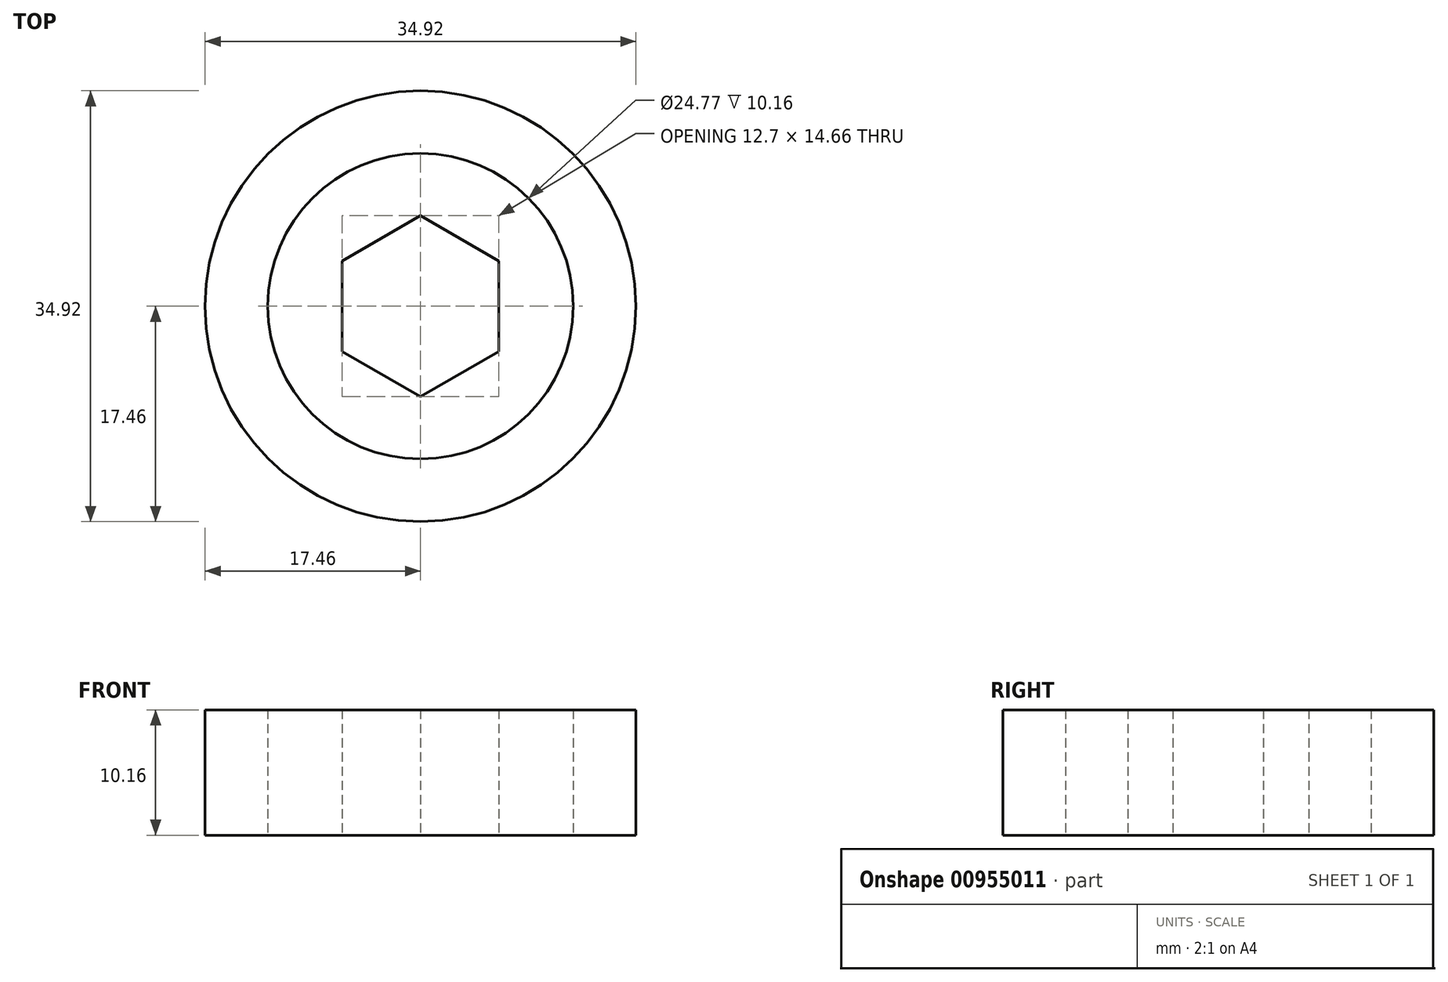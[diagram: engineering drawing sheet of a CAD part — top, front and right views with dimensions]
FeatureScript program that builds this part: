
annotation { "Feature Type Name" : "Feature", "Feature Type Description" : "" }
export const myFeature = defineFeature(function(context is Context, id is Id, definition is map)
    precondition{}
    {
        {
            var Q0;
            Q0=qCreatedBy(makeId("Top.planeOp"),FACE);
            var sketch = newSketch(context, id + "F0", { "sketchPlane" : qUnion([Q0])});
            skCircle(sketch, "E0", {"center": v(0, 0) * mm, "radius": 17.46 * mm});
            skCircle(sketch, "E1", {"center": v(0, 0) * mm, "radius": 12.38 * mm});
            skSolve(sketch);
        }
        {
            var Q0;
            Q0 = qSketchRegion(id + "F0", true);
            extrude(context, id + "F1", {"entities" : qUnion([Q0]), "depth" : 10.16 * mm, "offsetDistance" : 25.4 * mm});
        }
        {
            var Q0;
            Q0=qCreatedBy(makeId("Top.planeOp"),FACE);
            var sketch = newSketch(context, id + "F2", { "sketchPlane" : qUnion([Q0])});
            skCircle(sketch, "E2.cCircle", {"center": v(0, 0) * mm, "radius": 6.35 * mm, "construction": true});
            skLineSegment(sketch, "E2.0", {"start": v(0, 7.33) * mm, "end": v(6.35, 3.67) * mm});
            skLineSegment(sketch, "E2.1", {"start": v(6.35, 3.67) * mm, "end": v(6.35, -3.67) * mm});
            skLineSegment(sketch, "E2.2", {"start": v(6.35, -3.67) * mm, "end": v(0, -7.33) * mm});
            skLineSegment(sketch, "E2.3", {"start": v(0, -7.33) * mm, "end": v(-6.35, -3.67) * mm});
            skLineSegment(sketch, "E2.4", {"start": v(-6.35, -3.67) * mm, "end": v(-6.35, 3.67) * mm});
            skLineSegment(sketch, "E2.5", {"start": v(-6.35, 3.67) * mm, "end": v(0, 7.33) * mm});
            skPoint(sketch, "E2.0.midPoint", {"position": v(3.17, 5.5) * mm});
            skCircle(sketch, "E3.0", {"center": v(0, 0) * mm, "radius": 12.38 * mm});
            skSolve(sketch);
        }
        {
            var Q0;
            Q0 = qSketchRegion(id + "F2", true);
            extrude(context, id + "F3", {"entities" : qUnion([Q0]), "depth" : 10.16 * mm, "offsetDistance" : 25.4 * mm});
        }
    });
